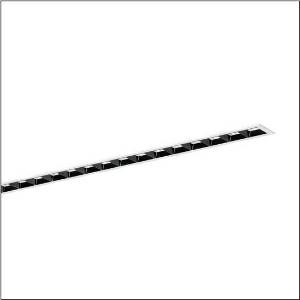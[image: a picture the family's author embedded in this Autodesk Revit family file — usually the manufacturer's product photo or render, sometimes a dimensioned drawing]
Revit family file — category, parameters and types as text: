
# Revit family: silica_r__21_51mx11tat4w_b1e5
name_source: partatom
category: Lighting Fixtures
units: mm (PartAtom-declared; Revit-internal decimal feet)

## family parameters
Cut with Voids When Loaded = No
Host = Face
Light Source = No
Part Type = Normal
Room Calculation Point = No
Round Connector Dimension = Use Diameter
Shared = No

## types (1)
- --- (1 x LED, 3720 lm, 32.2 W, 6500K)
    Apparent Load = 32 VA
    CIE Flux Codes = 85 99 100 100 100
    Color Rendering = 80
    Color Temperature = 6500K
    Default Elevation = 1800 mm
    Description = Silica® 21, office luminaire, primary light control with darklight reflector, of PMMA, black, CAT 2 (L<= 3000cd/m²), light emission: direct distribution, primary light characteristic: symmetric, installation type: recessed, LED, rated luminous flux: 3.720lm, luminous efficacy: 110lm/W, light colour: 8tw, colour temperature: 2700..6500K, with terminal, 3+2-pole, max. 2.5mm², mains connection: 220..240V, AC, 50/60Hz, rated input power: 33.8W, luminaire housing, of aluminium, traffic white (RAL 9016), length: 1.228mm, width: 79mm, height: 53mm, protection rating (complete): IP20, insulation class (complete): insulation class I (protective earthing), certification: CE, permissible operating ambient temperature: 0..+35°C, standard: EN 50419, packaging unit: 1 piece
    Height = 0 mm  [stored 0 ft]
    Lamp = 1 x LED
    Lamp Light Flux = 3720 lm
    Lamp Power = 32.2 W
    Lamp count = 1
    Length = 1227 mm
    Luminous efficacy = 116 lm/W
    Manufacturer = Siteco
    ModVariant = No
    Model = 51MX11TAT4W
    Mounting Place = Ceiling
    Mounting Type = Recessed
    Number of Poles = 1
    OnlyDefault = Yes
    Power Factor = 1
    Product Name = Silica® 21
    Product group = office luminaire | ceiling recessed
    ProductGroupID = 400
    Protection Class = Protection class I
    Protection Degree = IP 20
    RLX_Detail_Level = 1
    RlxData = <blob elided: 35641 chars, md5=8d6f16fe>
    Socket = socket
    Standby Power = 0 W
    System Light Flux = 3720 lm
    System Power = 32 W
    Type Comments = individual setting
    Type Image = l_1251632.jpg
    URL = http://relux.com
    VarID = @adj_046197
    Voltage = 0 V
    Weight = 0.00 kg
    Width = 79 mm

note: [stored X ft] marks values corroborated as IEEE doubles in the binary element streams (Revit-internal decimal feet)

## geometry (parser evidence)
native form markers: Blend x4, Sweep x9
no freeform markers — native parametric forms only
